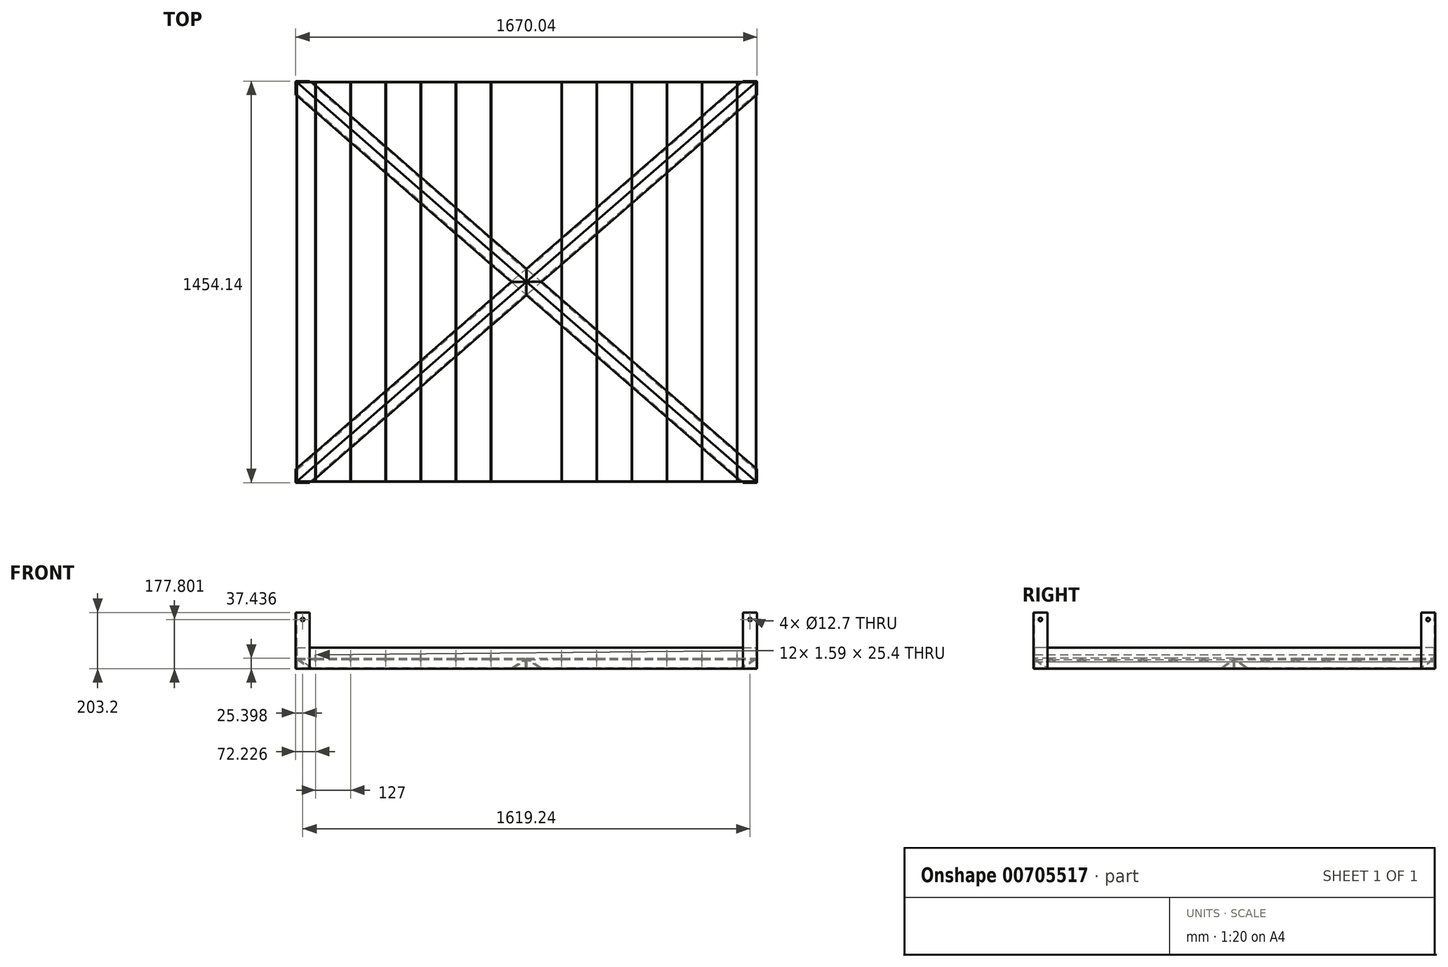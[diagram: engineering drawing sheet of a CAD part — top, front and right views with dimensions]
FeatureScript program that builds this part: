
annotation { "Feature Type Name" : "Feature", "Feature Type Description" : "" }
export const myFeature = defineFeature(function(context is Context, id is Id, definition is map)
    precondition{}
    {
        {
            var Q0;
            Q0=qCreatedBy(makeId("Top.planeOp"),FACE);
            var sketch = newSketch(context, id + "F0", { "sketchPlane" : qUnion([Q0])});
            skLineSegment(sketch, "E0.bottom", {"start": v(830.35, 722.4) * mm, "end": v(-830.35, 722.4) * mm});
            skLineSegment(sketch, "E0.top", {"start": v(830.35, -722.4) * mm, "end": v(-830.35, -722.4) * mm});
            skLineSegment(sketch, "E0.left", {"start": v(830.35, 722.4) * mm, "end": v(830.35, -722.4) * mm});
            skLineSegment(sketch, "E0.right", {"start": v(-830.35, 722.4) * mm, "end": v(-830.35, -722.4) * mm});
            skPoint(sketch, "E0.middle", {"position": v(0, 0) * mm});
            skSolve(sketch);
        }
        {
            var Q0;
            Q0=makeQuery(id+"F0.imprint","IMPRINT",FACE,{"disambiguationData":[TD([[makeQuery(id+"F0.imprint","IMPRINT",EDGE,{"derivedFrom":sQuery(id+"F0.wireOp",EDGE,"E0.bottom")}),1.0]])]});
            extrude(context, id + "F1", {"entities" : qUnion([Q0]), "oppositeDirection" : true, "depth" : 1.52 * mm, "offsetDistance" : 25.4 * mm});
        }
        {
            var Q0;
            Q0=makeQuery(id+"F1.opExtrude","CAP_FACE",FACE,{"disambiguationData":[OSD([sQuery(id+"F0.wireOp",EDGE,"E0.bottom"),sQuery(id+"F0.wireOp",EDGE,"E0.top"),sQuery(id+"F0.wireOp",EDGE,"E0.left"),sQuery(id+"F0.wireOp",EDGE,"E0.right")])],"isStart":false});
            cPlane(context, id + "F2", {"entities" : qUnion([Q0]), "cplaneType" : CPlaneType.OFFSET, "offset" : 0 * mm, "width" : 152.4 * mm, "height" : 152.4 * mm});
        }
        {
            var Q0;
            Q0=qCreatedBy(id+"F2.planeOp",FACE);
            var sketch = newSketch(context, id + "F3", { "sketchPlane" : qUnion([Q0])});
            skLineSegment(sketch, "E1.bottom", {"start": v(-830.35, -722.4) * mm, "end": v(830.35, -722.4) * mm});
            skLineSegment(sketch, "E1.top", {"start": v(-830.35, 722.4) * mm, "end": v(830.35, 722.4) * mm});
            skLineSegment(sketch, "E1.left", {"start": v(-830.35, -722.4) * mm, "end": v(-830.35, 722.4) * mm});
            skLineSegment(sketch, "E1.right", {"start": v(830.35, -722.4) * mm, "end": v(830.35, 722.4) * mm});
            skLineSegment(sketch, "E2.0", {"start": v(-831.85, -723.9) * mm, "end": v(-831.85, 723.9) * mm});
            skLineSegment(sketch, "E2.1", {"start": v(-831.85, -723.9) * mm, "end": v(831.85, -723.9) * mm});
            skLineSegment(sketch, "E2.2", {"start": v(831.85, -723.9) * mm, "end": v(831.85, 723.9) * mm});
            skLineSegment(sketch, "E2.3", {"start": v(-831.85, 723.9) * mm, "end": v(831.85, 723.9) * mm});
            skSolve(sketch);
        }
        {
            var Q0;
            Q0 = qSketchRegion(id + "F3", true);
            extrude(context, id + "F4", {"entities" : qUnion([Q0]), "operationType" : NewBodyOperationType.ADD, "oppositeDirection" : true, "depth" : 76.2 * mm, "offsetDistance" : 25.4 * mm});
        }
        {
            var Q0;
            Q0=makeQuery(id+"F1.opExtrude","CAP_FACE",FACE,{"disambiguationData":[OSD([sQuery(id+"F0.wireOp",EDGE,"E0.bottom"),sQuery(id+"F0.wireOp",EDGE,"E0.top"),sQuery(id+"F0.wireOp",EDGE,"E0.left"),sQuery(id+"F0.wireOp",EDGE,"E0.right")])],"isStart":true});
            cPlane(context, id + "F5", {"entities" : qUnion([Q0]), "cplaneType" : CPlaneType.OFFSET, "offset" : 0 * mm, "width" : 152.4 * mm, "height" : 152.4 * mm});
        }
        {
            var Q0;
            Q0=qCreatedBy(id+"F5.planeOp",FACE);
            var sketch = newSketch(context, id + "F6", { "sketchPlane" : qUnion([Q0])});
            skLineSegment(sketch, "E3", {"start": v(830.35, -722.4) * mm, "end": v(-830.35, 722.4) * mm});
            skLineSegment(sketch, "E4", {"start": v(830.35, 722.4) * mm, "end": v(-830.35, -722.4) * mm});
            skSolve(sketch);
        }
        {
            var Q0;
            Q0=sQuery(id+"F6.wireOp",EDGE,"E3");
            cPoint(context, id + "F7", {"entities" : qUnion([Q0]), "parameter" : 0.5});
        }
        {
            var Q0;
            Q0 = qCreatedBy(id + "F7" ,VERTEX);
            var Q1;
            Q1=sQuery(id+"F6.wireOp",EDGE,"E3");
            cPlane(context, id + "F8", {"entities" : qUnion([Q0, Q1]), "cplaneType" : CPlaneType.LINE_POINT, "offset" : 25.4 * mm, "width" : 152.4 * mm, "height" : 152.4 * mm});
        }
        {
            var Q0;
            Q0=sQuery(id+"F6.wireOp",EDGE,"E3");
            cPoint(context, id + "F9", {"entities" : qUnion([Q0]), "parameter" : 0.5});
        }
        {
            var Q0;
            Q0 = qCreatedBy(id + "F9" ,VERTEX);
            var Q1;
            Q1=sQuery(id+"F6.wireOp",EDGE,"E4");
            cPlane(context, id + "F10", {"entities" : qUnion([Q0, Q1]), "cplaneType" : CPlaneType.LINE_POINT, "offset" : 25.4 * mm, "width" : 152.4 * mm, "height" : 152.4 * mm});
        }
        {
            var Q0;
            Q0=qCreatedBy(id+"F8.planeOp",FACE);
            var sketch = newSketch(context, id + "F11", { "sketchPlane" : qUnion([Q0])});
            skLineSegment(sketch, "E5", {"start": v(0, 35.92) * mm, "end": v(0, 0) * mm});
            skLineSegment(sketch, "E6", {"start": v(0, 35.92) * mm, "end": v(35.92, 0) * mm});
            skLineSegment(sketch, "E7", {"start": v(0, 35.92) * mm, "end": v(-35.92, 0) * mm});
            skLineSegment(sketch, "E8", {"start": v(-17.96, 17.96) * mm, "end": v(-15.72, 15.71) * mm});
            skLineSegment(sketch, "E9", {"start": v(17.96, 17.96) * mm, "end": v(15.72, 15.71) * mm});
            skLineSegment(sketch, "E10", {"start": v(-15.72, 15.71) * mm, "end": v(-31.43, 0) * mm});
            skLineSegment(sketch, "E11", {"start": v(-15.72, 15.71) * mm, "end": v(0, 31.43) * mm});
            skLineSegment(sketch, "E12", {"start": v(15.72, 15.71) * mm, "end": v(31.43, 0) * mm});
            skLineSegment(sketch, "E13", {"start": v(15.72, 15.71) * mm, "end": v(-2.25, 33.67) * mm});
            skLineSegment(sketch, "E14", {"start": v(-35.92, 0) * mm, "end": v(-31.43, 0) * mm});
            skLineSegment(sketch, "E15", {"start": v(35.92, 0) * mm, "end": v(31.43, 0) * mm});
            skSolve(sketch);
        }
        {
            var Q0;
            Q0 = qSketchRegion(id + "F11", true);
            extrude(context, id + "F12", {"entities" : qUnion([Q0]), "operationType" : NewBodyOperationType.ADD, "endBound" : BoundingType.SYMMETRIC, "depth" : 2453.64 * mm, "offsetDistance" : 25.4 * mm});
        }
        {
            var Q0;
            Q0=qCreatedBy(id+"F10.planeOp",FACE);
            var sketch = newSketch(context, id + "F13", { "sketchPlane" : qUnion([Q0])});
            skLineSegment(sketch, "E16", {"start": v(0, 35.92) * mm, "end": v(0, 0) * mm});
            skLineSegment(sketch, "E17", {"start": v(0, 35.92) * mm, "end": v(35.92, 0) * mm});
            skLineSegment(sketch, "E18", {"start": v(0, 35.92) * mm, "end": v(-35.92, 0) * mm});
            skLineSegment(sketch, "E19", {"start": v(-17.96, 17.96) * mm, "end": v(-15.72, 15.71) * mm});
            skLineSegment(sketch, "E20", {"start": v(17.96, 17.96) * mm, "end": v(15.72, 15.71) * mm});
            skLineSegment(sketch, "E21", {"start": v(-15.72, 15.71) * mm, "end": v(-31.43, 0) * mm});
            skLineSegment(sketch, "E22", {"start": v(-15.72, 15.71) * mm, "end": v(0, 31.43) * mm});
            skLineSegment(sketch, "E23", {"start": v(15.72, 15.71) * mm, "end": v(31.43, 0) * mm});
            skLineSegment(sketch, "E24", {"start": v(15.72, 15.71) * mm, "end": v(-2.25, 33.67) * mm});
            skLineSegment(sketch, "E25", {"start": v(-35.92, 0) * mm, "end": v(-31.43, 0) * mm});
            skLineSegment(sketch, "E26", {"start": v(35.92, 0) * mm, "end": v(31.43, 0) * mm});
            skSolve(sketch);
        }
        {
            var Q0;
            Q0 = qSketchRegion(id + "F13", true);
            extrude(context, id + "F14", {"entities" : qUnion([Q0]), "operationType" : NewBodyOperationType.ADD, "endBound" : BoundingType.SYMMETRIC, "depth" : 2377.44 * mm, "offsetDistance" : 25.4 * mm});
        }
        {
            var Q0;
            Q0=qCreatedBy(id+"F2.planeOp",FACE);
            var sketch = newSketch(context, id + "F15", { "sketchPlane" : qUnion([Q0])});
            skLineSegment(sketch, "E27.bottom", {"start": v(-831.85, -723.9) * mm, "end": v(831.85, -723.9) * mm});
            skLineSegment(sketch, "E27.top", {"start": v(-831.85, 723.9) * mm, "end": v(831.85, 723.9) * mm});
            skLineSegment(sketch, "E27.left", {"start": v(-831.85, -723.9) * mm, "end": v(-831.85, 723.9) * mm});
            skLineSegment(sketch, "E27.right", {"start": v(831.85, -723.9) * mm, "end": v(831.85, 723.9) * mm});
            skLineSegment(sketch, "E28.0", {"start": v(-1040.13, -932.18) * mm, "end": v(1040.13, -932.18) * mm});
            skLineSegment(sketch, "E28.1", {"start": v(-1040.13, -932.18) * mm, "end": v(-1040.13, 932.18) * mm});
            skLineSegment(sketch, "E28.2", {"start": v(-1040.13, 932.18) * mm, "end": v(1040.13, 932.18) * mm});
            skLineSegment(sketch, "E28.3", {"start": v(1040.13, -932.18) * mm, "end": v(1040.13, 932.18) * mm});
            skSolve(sketch);
        }
        {
            var Q0;
            Q0=makeQuery(id+"F15.imprint","IMPRINT",FACE,{"disambiguationData":[TD([[makeQuery(id+"F15.imprint","IMPRINT",EDGE,{"derivedFrom":sQuery(id+"F15.wireOp",EDGE,"E27.bottom")}),-1.0]])]});
            var Q1;
            Q1 = qConstructionFilter(qBodyType(qCreatedBy(id + "F15" ,EDGE), BodyType.WIRE), ConstructionObject.NO);
            extrude(context, id + "F16", {"entities" : qUnion([Q0]), "operationType" : NewBodyOperationType.REMOVE, "surfaceEntities" : qUnion([Q1]), "oppositeDirection" : true, "depth" : 127 * mm, "offsetDistance" : 25.4 * mm});
        }
        {
            var Q0;
            {var subQ1=makeQuery(id+"F12.opExtrude","SWEPT_FACE",FACE,{"disambiguationData":[OSD([sQuery(id+"F11.wireOp",EDGE,"E7")])]});Q0=makeQuery(id+"F14.boolean.opBoolean","SPLIT",FACE,{"disambiguationData":[TD([makeQuery(id+"F14.opExtrude","SWEPT_FACE",FACE,{"disambiguationData":[OSD([sQuery(id+"F13.wireOp",EDGE,"E18")])]})])],"derivedFrom":makeQuery(id+"F12.boolean.opBoolean","SPLIT",FACE,{"disambiguationData":[TD([subQ1])],"derivedFrom":makeQuery(id+"F1.opExtrude","CAP_FACE",FACE,{"disambiguationData":[OSD([sQuery(id+"F0.wireOp",EDGE,"E0.bottom"),sQuery(id+"F0.wireOp",EDGE,"E0.top"),sQuery(id+"F0.wireOp",EDGE,"E0.left"),sQuery(id+"F0.wireOp",EDGE,"E0.right")])],"isStart":true})})});}
            cPlane(context, id + "F17", {"entities" : qUnion([Q0]), "cplaneType" : CPlaneType.OFFSET, "offset" : 35.92 * mm, "width" : 152.4 * mm, "height" : 152.4 * mm});
        }
        {
            var Q0;
            Q0=qCreatedBy(id+"F17.planeOp",FACE);
            var sketch = newSketch(context, id + "F18", { "sketchPlane" : qUnion([Q0])});
            skLineSegment(sketch, "E29", {"start": v(0, -722.4) * mm, "end": v(0, 722.4) * mm, "construction": true});
            skLineSegment(sketch, "E30.bottom", {"start": v(-127, -722.4) * mm, "end": v(-128.59, -722.4) * mm});
            skLineSegment(sketch, "E30.top", {"start": v(-127, 722.4) * mm, "end": v(-128.59, 722.4) * mm});
            skLineSegment(sketch, "E30.left", {"start": v(-127, -722.4) * mm, "end": v(-127, 722.4) * mm});
            skLineSegment(sketch, "E30.right", {"start": v(-128.59, -722.4) * mm, "end": v(-128.59, 722.4) * mm});
            skLineSegment(sketch, "E31.1.0.0", {"start": v(-255.59, -722.4) * mm, "end": v(-255.59, 722.4) * mm});
            skLineSegment(sketch, "E31.1.0.1", {"start": v(-254, -722.4) * mm, "end": v(-255.59, -722.4) * mm});
            skLineSegment(sketch, "E31.1.0.2", {"start": v(-254, -722.4) * mm, "end": v(-254, 722.4) * mm});
            skLineSegment(sketch, "E31.1.0.3", {"start": v(-254, 722.4) * mm, "end": v(-255.59, 722.4) * mm});
            skLineSegment(sketch, "E31.2.0.0", {"start": v(-382.59, -722.4) * mm, "end": v(-382.59, 722.4) * mm});
            skLineSegment(sketch, "E31.2.0.1", {"start": v(-381, -722.4) * mm, "end": v(-382.59, -722.4) * mm});
            skLineSegment(sketch, "E31.2.0.2", {"start": v(-381, -722.4) * mm, "end": v(-381, 722.4) * mm});
            skLineSegment(sketch, "E31.2.0.3", {"start": v(-381, 722.4) * mm, "end": v(-382.59, 722.4) * mm});
            skLineSegment(sketch, "E31.3.0.0", {"start": v(-509.59, -722.4) * mm, "end": v(-509.59, 722.4) * mm});
            skLineSegment(sketch, "E31.3.0.1", {"start": v(-508, -722.4) * mm, "end": v(-509.59, -722.4) * mm});
            skLineSegment(sketch, "E31.3.0.2", {"start": v(-508, -722.4) * mm, "end": v(-508, 722.4) * mm});
            skLineSegment(sketch, "E31.3.0.3", {"start": v(-508, 722.4) * mm, "end": v(-509.59, 722.4) * mm});
            skLineSegment(sketch, "E31.4.0.0", {"start": v(-636.59, -722.4) * mm, "end": v(-636.59, 722.4) * mm});
            skLineSegment(sketch, "E31.4.0.1", {"start": v(-635, -722.4) * mm, "end": v(-636.59, -722.4) * mm});
            skLineSegment(sketch, "E31.4.0.2", {"start": v(-635, -722.4) * mm, "end": v(-635, 722.4) * mm});
            skLineSegment(sketch, "E31.4.0.3", {"start": v(-635, 722.4) * mm, "end": v(-636.59, 722.4) * mm});
            skLineSegment(sketch, "E31.5.0.0", {"start": v(-763.59, -722.4) * mm, "end": v(-763.59, 722.4) * mm});
            skLineSegment(sketch, "E31.5.0.1", {"start": v(-762, -722.4) * mm, "end": v(-763.59, -722.4) * mm});
            skLineSegment(sketch, "E31.5.0.2", {"start": v(-762, -722.4) * mm, "end": v(-762, 722.4) * mm});
            skLineSegment(sketch, "E31.5.0.3", {"start": v(-762, 722.4) * mm, "end": v(-763.59, 722.4) * mm});
            skLineSegment(sketch, "E31.direction1", {"start": v(-128.59, -722.4) * mm, "end": v(-255.59, -722.4) * mm, "construction": true});
            skLineSegment(sketch, "E32.MirrorCS", {"start": v(127, -722.4) * mm, "end": v(128.59, -722.4) * mm});
            skLineSegment(sketch, "E33.MirrorCS", {"start": v(254, -722.4) * mm, "end": v(255.59, -722.4) * mm});
            skLineSegment(sketch, "E34.MirrorCS", {"start": v(508, -722.4) * mm, "end": v(509.59, -722.4) * mm});
            skLineSegment(sketch, "E35.MirrorCS", {"start": v(381, -722.4) * mm, "end": v(382.59, -722.4) * mm});
            skLineSegment(sketch, "E36.MirrorCS", {"start": v(762, -722.4) * mm, "end": v(763.59, -722.4) * mm});
            skLineSegment(sketch, "E37.MirrorCS", {"start": v(762, 722.4) * mm, "end": v(763.59, 722.4) * mm});
            skLineSegment(sketch, "E38.MirrorCS", {"start": v(635, -722.4) * mm, "end": v(636.59, -722.4) * mm});
            skLineSegment(sketch, "E39.MirrorCS", {"start": v(762, -722.4) * mm, "end": v(762, 722.4) * mm});
            skLineSegment(sketch, "E40.MirrorCS", {"start": v(763.59, -722.4) * mm, "end": v(763.59, 722.4) * mm});
            skLineSegment(sketch, "E41.MirrorCS", {"start": v(128.59, -722.4) * mm, "end": v(255.59, -722.4) * mm, "construction": true});
            skLineSegment(sketch, "E42.MirrorCS", {"start": v(381, 722.4) * mm, "end": v(382.59, 722.4) * mm});
            skLineSegment(sketch, "E43.MirrorCS", {"start": v(508, 722.4) * mm, "end": v(509.59, 722.4) * mm});
            skLineSegment(sketch, "E44.MirrorCS", {"start": v(254, 722.4) * mm, "end": v(255.59, 722.4) * mm});
            skLineSegment(sketch, "E45.MirrorCS", {"start": v(127, 722.4) * mm, "end": v(128.59, 722.4) * mm});
            skLineSegment(sketch, "E46.MirrorCS", {"start": v(635, 722.4) * mm, "end": v(636.59, 722.4) * mm});
            skLineSegment(sketch, "E47.MirrorCS", {"start": v(382.59, -722.4) * mm, "end": v(382.59, 722.4) * mm});
            skLineSegment(sketch, "E48.MirrorCS", {"start": v(508, -722.4) * mm, "end": v(508, 722.4) * mm});
            skLineSegment(sketch, "E49.MirrorCS", {"start": v(635, -722.4) * mm, "end": v(635, 722.4) * mm});
            skLineSegment(sketch, "E50.MirrorCS", {"start": v(127, -722.4) * mm, "end": v(127, 722.4) * mm});
            skLineSegment(sketch, "E51.MirrorCS", {"start": v(255.59, -722.4) * mm, "end": v(255.59, 722.4) * mm});
            skLineSegment(sketch, "E52.MirrorCS", {"start": v(509.59, -722.4) * mm, "end": v(509.59, 722.4) * mm});
            skLineSegment(sketch, "E53.MirrorCS", {"start": v(636.59, -722.4) * mm, "end": v(636.59, 722.4) * mm});
            skLineSegment(sketch, "E54.MirrorCS", {"start": v(381, -722.4) * mm, "end": v(381, 722.4) * mm});
            skLineSegment(sketch, "E55.MirrorCS", {"start": v(254, -722.4) * mm, "end": v(254, 722.4) * mm});
            skLineSegment(sketch, "E56.MirrorCS", {"start": v(128.59, -722.4) * mm, "end": v(128.59, 722.4) * mm});
            skSolve(sketch);
        }
        {
            var Q0;
            Q0=makeQuery(id+"F18.imprint","IMPRINT",FACE,{"disambiguationData":[TD([[makeQuery(id+"F18.imprint","IMPRINT",EDGE,{"derivedFrom":sQuery(id+"F18.wireOp",EDGE,"E30.bottom")}),-1.0]])]});
            var Q1;
            Q1=makeQuery(id+"F18.imprint","IMPRINT",FACE,{"disambiguationData":[TD([[makeQuery(id+"F18.imprint","IMPRINT",EDGE,{"derivedFrom":sQuery(id+"F18.wireOp",EDGE,"E31.1.0.0")}),-1.0]])]});
            var Q2;
            Q2=makeQuery(id+"F18.imprint","IMPRINT",FACE,{"disambiguationData":[TD([[makeQuery(id+"F18.imprint","IMPRINT",EDGE,{"derivedFrom":sQuery(id+"F18.wireOp",EDGE,"E31.2.0.0")}),-1.0]])]});
            var Q3;
            Q3=makeQuery(id+"F18.imprint","IMPRINT",FACE,{"disambiguationData":[TD([[makeQuery(id+"F18.imprint","IMPRINT",EDGE,{"derivedFrom":sQuery(id+"F18.wireOp",EDGE,"E31.4.0.0")}),-1.0]])]});
            var Q4;
            Q4=makeQuery(id+"F18.imprint","IMPRINT",FACE,{"disambiguationData":[TD([[makeQuery(id+"F18.imprint","IMPRINT",EDGE,{"derivedFrom":sQuery(id+"F18.wireOp",EDGE,"E31.5.0.0")}),-1.0]])]});
            var Q5;
            Q5=makeQuery(id+"F18.imprint","IMPRINT",FACE,{"disambiguationData":[TD([[makeQuery(id+"F18.imprint","IMPRINT",EDGE,{"derivedFrom":sQuery(id+"F18.wireOp",EDGE,"E33.MirrorCS")}),1.0]])]});
            var Q6;
            Q6=makeQuery(id+"F18.imprint","IMPRINT",FACE,{"disambiguationData":[TD([[makeQuery(id+"F18.imprint","IMPRINT",EDGE,{"derivedFrom":sQuery(id+"F18.wireOp",EDGE,"E32.MirrorCS")}),1.0]])]});
            var Q7;
            Q7=makeQuery(id+"F18.imprint","IMPRINT",FACE,{"disambiguationData":[TD([[makeQuery(id+"F18.imprint","IMPRINT",EDGE,{"derivedFrom":sQuery(id+"F18.wireOp",EDGE,"E42.MirrorCS")}),-1.0]])]});
            var Q8;
            Q8=makeQuery(id+"F18.imprint","IMPRINT",FACE,{"disambiguationData":[TD([[makeQuery(id+"F18.imprint","IMPRINT",EDGE,{"derivedFrom":sQuery(id+"F18.wireOp",EDGE,"E43.MirrorCS")}),-1.0]])]});
            var Q9;
            Q9=makeQuery(id+"F18.imprint","IMPRINT",FACE,{"disambiguationData":[TD([[makeQuery(id+"F18.imprint","IMPRINT",EDGE,{"derivedFrom":sQuery(id+"F18.wireOp",EDGE,"E36.MirrorCS")}),1.0]])]});
            var Q10;
            Q10=makeQuery(id+"F18.imprint","IMPRINT",FACE,{"disambiguationData":[TD([[makeQuery(id+"F18.imprint","IMPRINT",EDGE,{"derivedFrom":sQuery(id+"F18.wireOp",EDGE,"E46.MirrorCS")}),-1.0]])]});
            var Q11;
            Q11=makeQuery(id+"F18.imprint","IMPRINT",FACE,{"disambiguationData":[TD([[makeQuery(id+"F18.imprint","IMPRINT",EDGE,{"derivedFrom":sQuery(id+"F18.wireOp",EDGE,"E31.3.0.0")}),-1.0]])]});
            extrude(context, id + "F19", {"entities" : qUnion([Q0, Q1, Q2, Q3, Q4, Q5, Q6, Q7, Q8, Q9, Q10, Q11]), "operationType" : NewBodyOperationType.ADD, "endBound" : BoundingType.SYMMETRIC, "oppositeDirection" : true, "depth" : 25.4 * mm, "offsetDistance" : 25.4 * mm});
        }
        {
            var Q0;
            Q0=qCreatedBy(id+"F2.planeOp",FACE);
            var sketch = newSketch(context, id + "F20", { "sketchPlane" : qUnion([Q0])});
            skLineSegment(sketch, "E57", {"start": v(784.22, 723.9) * mm, "end": v(831.85, 723.9) * mm});
            skLineSegment(sketch, "E58", {"start": v(831.85, 723.9) * mm, "end": v(831.85, 676.27) * mm});
            skLineSegment(sketch, "E59", {"start": v(831.85, 676.27) * mm, "end": v(835.02, 676.27) * mm});
            skLineSegment(sketch, "E60", {"start": v(835.02, 676.27) * mm, "end": v(835.02, 727.07) * mm});
            skLineSegment(sketch, "E61", {"start": v(784.22, 727.07) * mm, "end": v(784.22, 723.9) * mm});
            skLineSegment(sketch, "E62", {"start": v(835.02, 727.07) * mm, "end": v(784.22, 727.07) * mm});
            skLineSegment(sketch, "E63", {"start": v(0, -722.4) * mm, "end": v(0, 722.4) * mm, "construction": true});
            skLineSegment(sketch, "E64", {"start": v(-830.35, 0) * mm, "end": v(830.35, 0) * mm, "construction": true});
            skLineSegment(sketch, "E65.MirrorCS", {"start": v(-835.02, 676.27) * mm, "end": v(-835.02, 727.07) * mm});
            skLineSegment(sketch, "E66.MirrorCS", {"start": v(-831.85, 676.27) * mm, "end": v(-835.02, 676.27) * mm});
            skLineSegment(sketch, "E67.MirrorCS", {"start": v(-835.02, 727.07) * mm, "end": v(-784.22, 727.07) * mm});
            skLineSegment(sketch, "E68.MirrorCS", {"start": v(-784.22, 727.07) * mm, "end": v(-784.22, 723.9) * mm});
            skLineSegment(sketch, "E69.MirrorCS", {"start": v(-784.22, 723.9) * mm, "end": v(-831.85, 723.9) * mm});
            skLineSegment(sketch, "E70.MirrorCS", {"start": v(-831.85, 723.9) * mm, "end": v(-831.85, 676.27) * mm});
            skLineSegment(sketch, "E71.MirrorCS", {"start": v(-831.85, -676.27) * mm, "end": v(-835.02, -676.27) * mm});
            skLineSegment(sketch, "E72.MirrorCS", {"start": v(-835.02, -676.27) * mm, "end": v(-835.02, -727.07) * mm});
            skLineSegment(sketch, "E73.MirrorCS", {"start": v(-784.22, -727.07) * mm, "end": v(-784.22, -723.9) * mm});
            skLineSegment(sketch, "E74.MirrorCS", {"start": v(-835.02, -727.07) * mm, "end": v(-784.22, -727.07) * mm});
            skLineSegment(sketch, "E75.MirrorCS", {"start": v(-784.22, -723.9) * mm, "end": v(-831.85, -723.9) * mm});
            skLineSegment(sketch, "E76.MirrorCS", {"start": v(784.22, -723.9) * mm, "end": v(831.85, -723.9) * mm});
            skLineSegment(sketch, "E77.MirrorCS", {"start": v(-831.85, -723.9) * mm, "end": v(-831.85, -676.27) * mm});
            skLineSegment(sketch, "E78.MirrorCS", {"start": v(831.85, -676.27) * mm, "end": v(835.02, -676.27) * mm});
            skLineSegment(sketch, "E79.MirrorCS", {"start": v(784.22, -727.07) * mm, "end": v(784.22, -723.9) * mm});
            skLineSegment(sketch, "E80.MirrorCS", {"start": v(831.85, -723.9) * mm, "end": v(831.85, -676.27) * mm});
            skLineSegment(sketch, "E81.MirrorCS", {"start": v(835.02, -676.27) * mm, "end": v(835.02, -727.07) * mm});
            skLineSegment(sketch, "E82.MirrorCS", {"start": v(835.02, -727.07) * mm, "end": v(784.22, -727.07) * mm});
            skSolve(sketch);
        }
        {
            var Q0;
            Q0 = qSketchRegion(id + "F20", true);
            extrude(context, id + "F21", {"entities" : qUnion([Q0]), "operationType" : NewBodyOperationType.ADD, "oppositeDirection" : true, "depth" : 203.2 * mm, "offsetDistance" : 25.4 * mm});
        }
        {
            var Q0;
            Q0=qCreatedBy(makeId("Right.planeOp"),FACE);
            var sketch = newSketch(context, id + "F22", { "sketchPlane" : qUnion([Q0])});
            skLineSegment(sketch, "E83", {"start": v(-701.67, 201.68) * mm, "end": v(-701.67, 176.28) * mm, "construction": true});
            skLineSegment(sketch, "E84", {"start": v(701.67, 201.68) * mm, "end": v(701.67, 176.28) * mm, "construction": true});
            skCircle(sketch, "E85", {"center": v(-701.67, 176.28) * mm, "radius": 6.35 * mm});
            skCircle(sketch, "E86", {"center": v(701.67, 176.28) * mm, "radius": 6.35 * mm});
            skSolve(sketch);
        }
        {
            var Q0;
            Q0 = qSketchRegion(id + "F22", true);
            extrude(context, id + "F23", {"entities" : qUnion([Q0]), "operationType" : NewBodyOperationType.REMOVE, "endBound" : BoundingType.SYMMETRIC, "depth" : 2405.89 * mm, "offsetDistance" : 25.4 * mm});
        }
        {
            var Q0;
            Q0=qCreatedBy(makeId("Front.planeOp"),FACE);
            var sketch = newSketch(context, id + "F24", { "sketchPlane" : qUnion([Q0])});
            skLineSegment(sketch, "E87", {"start": v(-809.62, 201.68) * mm, "end": v(-809.62, 176.28) * mm, "construction": true});
            skLineSegment(sketch, "E88", {"start": v(809.62, 201.68) * mm, "end": v(809.62, 176.28) * mm, "construction": true});
            skCircle(sketch, "E89", {"center": v(-809.62, 176.28) * mm, "radius": 6.35 * mm});
            skCircle(sketch, "E90", {"center": v(809.62, 176.28) * mm, "radius": 6.35 * mm});
            skSolve(sketch);
        }
        {
            var Q0;
            Q0 = qSketchRegion(id + "F24", true);
            extrude(context, id + "F25", {"entities" : qUnion([Q0]), "operationType" : NewBodyOperationType.REMOVE, "endBound" : BoundingType.SYMMETRIC, "depth" : 2346.96 * mm, "offsetDistance" : 25.4 * mm});
        }
    });
